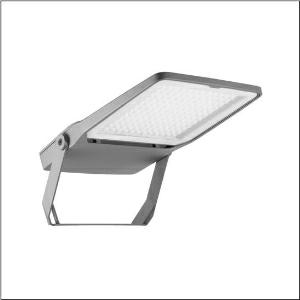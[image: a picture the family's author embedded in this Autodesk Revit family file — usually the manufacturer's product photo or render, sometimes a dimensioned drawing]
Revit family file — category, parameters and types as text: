
# Revit family: floodlight_fl_20_midi___rs17_5xa7682d2b1ac_83de
name_source: partatom
category: Lighting Fixtures
units: mm (PartAtom-declared; Revit-internal decimal feet)

## family parameters
Cut with Voids When Loaded = No
Host = Face
Light Source = No
Part Type = Normal
Room Calculation Point = No
Round Connector Dimension = Use Diameter
Shared = No

## types (1)
- --- (1 x LED 4000K / CRI = 70 (unbekannt), 19540 lm, 4000K)
    Apparent Load = 142 VA
    CIE Flux Codes = 79 92 99 100 100
    Color Rendering = 70
    Color Temperature = 4000K
    Default Elevation = 1800 mm
    Description = Floodlight FL 20 midi, floodlight, primary light control with lens, of plastic, primary optical cover: protective disc, of toughened safety glass, transparent, light distribution: RS17, light emission: direct distribution, primary light characteristic: rotationally symmetric, installation type: surface-mounted, LED, High Power LED, rated luminous flux: 19.540lm, luminous efficacy: 138lm/W, light colour: 740, colour temperature: 4000K, control gear: ECG Plus, control: flexible luminous flux parameterisation, time-dependent luminous flux control, digital communication interface, power reduction, overheat protection, electronic power reduction, with terminal, 5-pole, max. 2.5mm², mains connection: 220..240V, AC, 50/60Hz, rated input power: 142W, LED unit, of diecast aluminium, powder-coated, Siteco® metallic grey (DB 702S), corrosivity category C5 mid according to DIN EN ISO 12944, incl. 1x M20 cable gland for cable Ø 6.5..12mm, length: 654mm, width: 450mm, height: 76mm, housing frame, of diecast aluminium, powder-coated, Siteco® metallic grey (DB 702S), mounting bracket, of steel, powder-coated, Siteco® metallic grey (DB 702S), DALI, protection rating (complete): IP66, insulation class (complete): insulation class II (safety insulation), certification: CE, ENEC, VDE, protection symbol: D, permissible operating ambient temperature: -40..+40°C, permissible operating ambient temperature for outdoor applications: -40..+50°C, standard: DIN EN 12944, packaging unit: 1 piece

Light Distribution: RS17
    Height = 76 mm
    Lamp = 1 x LED 4000K / CRI >= 70 (unbekannt)
    Lamp Light Flux = 19540 lm
    Lamp count = 1
    Length = 672 mm
    Luminous efficacy = 138 lm/W
    Manufacturer = Siteco
    ModVariant = No
    Model = 5XA7682D2B1AC
    Mounting Place = Wall
    Mounting Type = Surface mounted
    Number of Poles = 1
    OnlyDefault = Yes
    Power Factor = 1
    Product Name = Floodlight FL 20 midi | RS17
    Product group = floodlight | wall mounted
    ProductGroupID = 2001
    Protection Class = Protection class II
    Protection Degree = IP 66
    RLX_Detail_Level = 1
    RLX_Emergency_Light_Flux = 0 lm
    RLX_Emergency_Type = 0
    RLX_Emergency_Type_DB = No
    RlxData = <blob elided: 92317 chars, md5=1974a1c1>
    Socket = socket
    Standby Power = 0 W
    System Light Flux = 19540 lm
    System Power = 142 W
    Type Comments = factory setting: luminous flux: 100 % | dim-lin: 254 | 489 mA
    Type Image = l_1005943.jpg
    URL = http://relux.com
    VarID = @adj_146665
    Voltage = 0 V
    Weight = 0.00 kg
    Width = 450 mm

## geometry (parser evidence)
native form markers: Blend x4, Sweep x13
no freeform markers — native parametric forms only
